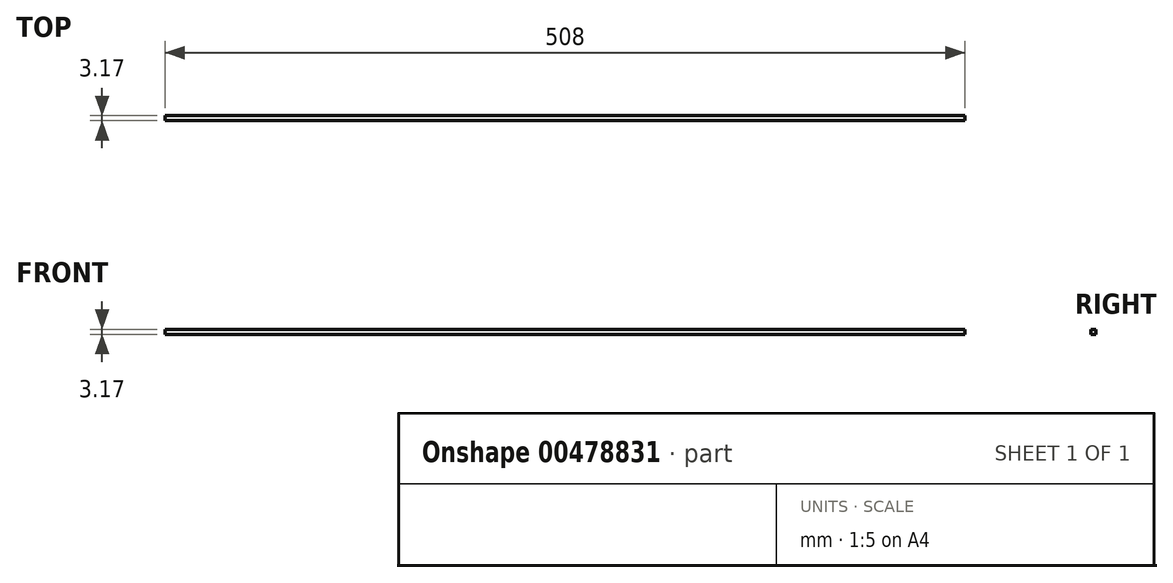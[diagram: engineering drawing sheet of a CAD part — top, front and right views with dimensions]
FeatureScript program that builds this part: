
annotation { "Feature Type Name" : "Feature", "Feature Type Description" : "" }
export const myFeature = defineFeature(function(context is Context, id is Id, definition is map)
    precondition{}
    {
        {
            var Q0;
            Q0=qCreatedBy(makeId("Front.planeOp"),FACE);
            var sketch = newSketch(context, id + "F0", { "sketchPlane" : qUnion([Q0])});
            skLineSegment(sketch, "E0.bottom", {"start": v(-59.14, 45.33) * mm, "end": v(448.86, 45.33) * mm});
            skLineSegment(sketch, "E0.top", {"start": v(-59.14, 42.16) * mm, "end": v(448.86, 42.16) * mm});
            skLineSegment(sketch, "E0.left", {"start": v(-59.14, 45.33) * mm, "end": v(-59.14, 42.16) * mm});
            skLineSegment(sketch, "E0.right", {"start": v(448.86, 45.33) * mm, "end": v(448.86, 42.16) * mm});
            skSolve(sketch);
        }
        {
            var Q0;
            Q0=makeQuery(id+"F0.imprint","IMPRINT",FACE,{"disambiguationData":[TD([[makeQuery(id+"F0.imprint","IMPRINT",EDGE,{"derivedFrom":sQuery(id+"F0.wireOp",EDGE,"E0.bottom")}),-1.0]])]});
            extrude(context, id + "F1", {"entities" : qUnion([Q0]), "depth" : 3.17 * mm});
        }
    });
